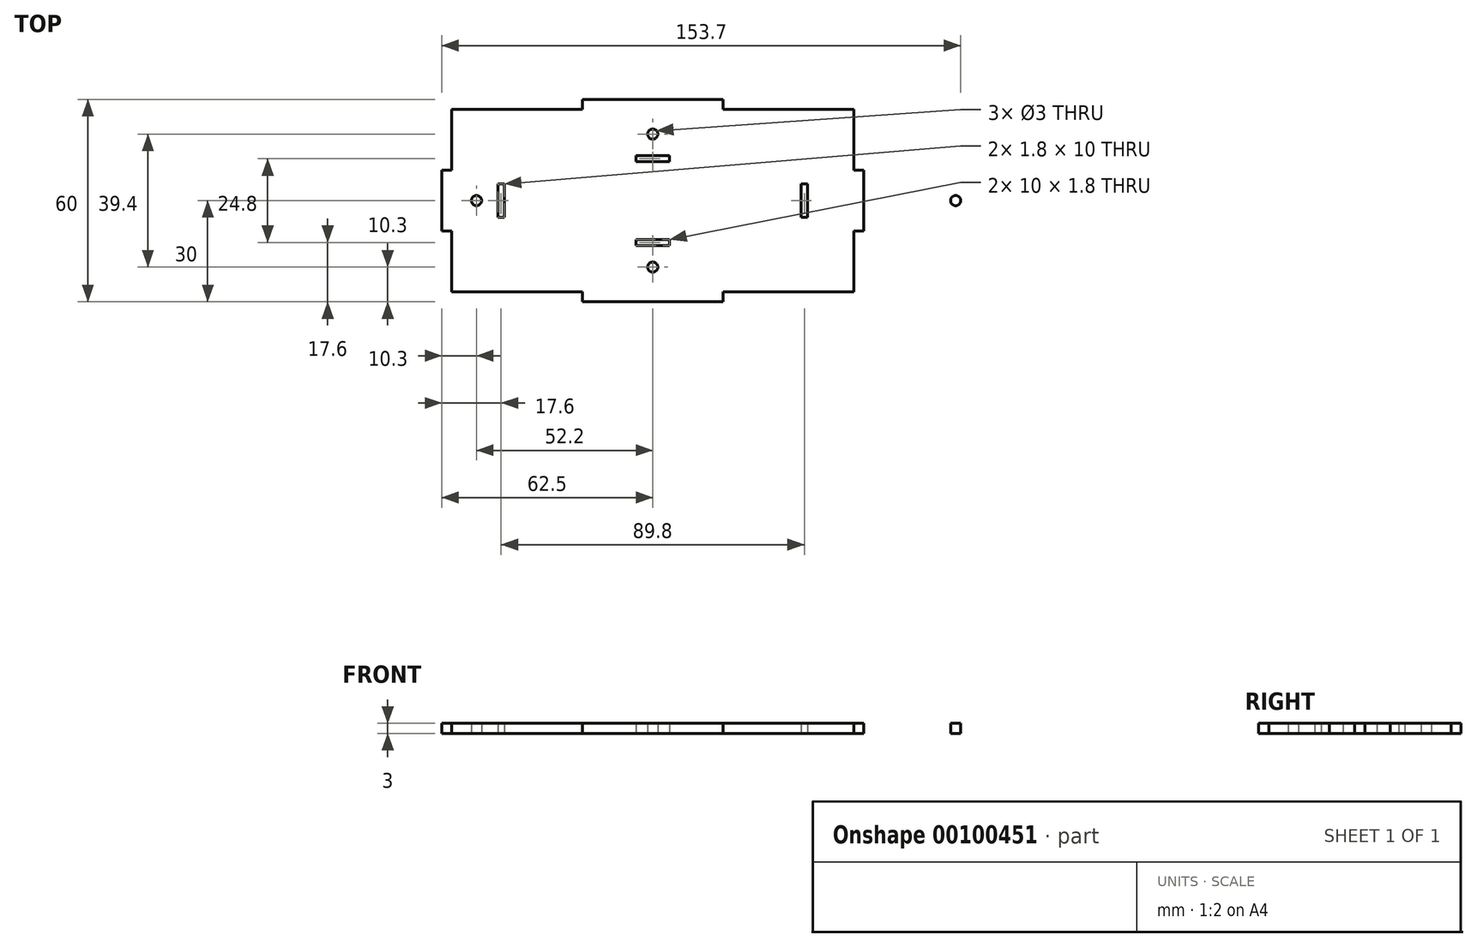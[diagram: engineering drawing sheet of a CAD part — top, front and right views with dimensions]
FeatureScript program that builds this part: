
annotation { "Feature Type Name" : "Feature", "Feature Type Description" : "" }
export const myFeature = defineFeature(function(context is Context, id is Id, definition is map)
    precondition{}
    {
        {
            var Q0;
            Q0=qCreatedBy(makeId("Top.planeOp"),FACE);
            var sketch = newSketch(context, id + "F0", { "sketchPlane" : qUnion([Q0])});
            skLineSegment(sketch, "E0.bottom", {"start": v(-59.5, 27) * mm, "end": v(-20.83, 27) * mm});
            skLineSegment(sketch, "E0.top", {"start": v(-59.5, -27) * mm, "end": v(-20.83, -27) * mm});
            skLineSegment(sketch, "E0.left", {"start": v(-59.5, 27) * mm, "end": v(-59.5, 9) * mm});
            skLineSegment(sketch, "E0.right", {"start": v(59.5, 27) * mm, "end": v(59.5, 9) * mm});
            skLineSegment(sketch, "E1.bottom", {"start": v(-59.5, 9) * mm, "end": v(-62.5, 9) * mm});
            skLineSegment(sketch, "E1.top", {"start": v(-59.5, -9) * mm, "end": v(-62.5, -9) * mm});
            skLineSegment(sketch, "E1.right", {"start": v(-62.5, 9) * mm, "end": v(-62.5, -9) * mm});
            skLineSegment(sketch, "E2.top", {"start": v(-20.83, 30) * mm, "end": v(20.83, 30) * mm});
            skLineSegment(sketch, "E2.left", {"start": v(-20.83, 27) * mm, "end": v(-20.83, 30) * mm});
            skLineSegment(sketch, "E2.right", {"start": v(20.83, 27) * mm, "end": v(20.83, 30) * mm});
            skLineSegment(sketch, "E3.bottom", {"start": v(59.5, 9) * mm, "end": v(62.5, 9) * mm});
            skLineSegment(sketch, "E3.top", {"start": v(59.5, -9) * mm, "end": v(62.5, -9) * mm});
            skLineSegment(sketch, "E3.right", {"start": v(62.5, 9) * mm, "end": v(62.5, -9) * mm});
            skLineSegment(sketch, "E4.top", {"start": v(20.83, -30) * mm, "end": v(-20.83, -30) * mm});
            skLineSegment(sketch, "E4.left", {"start": v(20.83, -27) * mm, "end": v(20.83, -30) * mm});
            skLineSegment(sketch, "E4.right", {"start": v(-20.83, -27) * mm, "end": v(-20.83, -30) * mm});
            skLineSegment(sketch, "E5.trimOffspring", {"start": v(20.83, 27) * mm, "end": v(59.5, 27) * mm});
            skLineSegment(sketch, "E6.trimOffspring", {"start": v(20.83, -27) * mm, "end": v(59.5, -27) * mm});
            skLineSegment(sketch, "E7.trimOffspring", {"start": v(-59.5, -9) * mm, "end": v(-59.5, -27) * mm});
            skLineSegment(sketch, "E8.trimOffspring", {"start": v(59.5, -9) * mm, "end": v(59.5, -27) * mm});
            skLineSegment(sketch, "E9", {"start": v(-62.5, 30) * mm, "end": v(-20.83, 30) * mm, "construction": true});
            skLineSegment(sketch, "E10", {"start": v(20.83, 30) * mm, "end": v(62.5, 30) * mm, "construction": true});
            skCircle(sketch, "E11", {"center": v(-52.2, 0) * mm, "radius": 1.5 * mm});
            skLineSegment(sketch, "E12.bottom", {"start": v(-45.8, 5) * mm, "end": v(-44, 5) * mm});
            skLineSegment(sketch, "E12.top", {"start": v(-45.8, -5) * mm, "end": v(-44, -5) * mm});
            skLineSegment(sketch, "E12.left", {"start": v(-45.8, 5) * mm, "end": v(-45.8, -5) * mm});
            skLineSegment(sketch, "E12.right", {"start": v(-44, 5) * mm, "end": v(-44, -5) * mm});
            skLineSegment(sketch, "E13.MirrorCS", {"start": v(45.8, 5) * mm, "end": v(44, 5) * mm});
            skLineSegment(sketch, "E14.MirrorCS", {"start": v(45.8, -5) * mm, "end": v(44, -5) * mm});
            skLineSegment(sketch, "E15.MirrorCS", {"start": v(44, 5) * mm, "end": v(44, -5) * mm});
            skLineSegment(sketch, "E16.MirrorCS", {"start": v(45.8, 5) * mm, "end": v(45.8, -5) * mm});
            skCircle(sketch, "E17.MirrorC", {"center": v(89.7, 0) * mm, "radius": 1.5 * mm});
            skCircle(sketch, "E18", {"center": v(0, 19.7) * mm, "radius": 1.5 * mm});
            skLineSegment(sketch, "E19.bottom", {"start": v(5, 13.3) * mm, "end": v(-5, 13.3) * mm});
            skLineSegment(sketch, "E19.top", {"start": v(5, 11.5) * mm, "end": v(-5, 11.5) * mm});
            skLineSegment(sketch, "E19.left", {"start": v(5, 13.3) * mm, "end": v(5, 11.5) * mm});
            skLineSegment(sketch, "E19.right", {"start": v(-5, 13.3) * mm, "end": v(-5, 11.5) * mm});
            skLineSegment(sketch, "E20.MirrorCS", {"start": v(-5, -13.3) * mm, "end": v(-5, -11.5) * mm});
            skLineSegment(sketch, "E21.MirrorCS", {"start": v(5, -13.3) * mm, "end": v(5, -11.5) * mm});
            skCircle(sketch, "E22.MirrorC", {"center": v(0, -19.7) * mm, "radius": 1.5 * mm});
            skLineSegment(sketch, "E23.MirrorCS", {"start": v(5, -11.5) * mm, "end": v(-5, -11.5) * mm});
            skLineSegment(sketch, "E24.MirrorCS", {"start": v(5, -13.3) * mm, "end": v(-5, -13.3) * mm});
            skSolve(sketch);
        }
        {
            var Q0;
            Q0=qSketchRegion(id+"F0",true);
            extrude(context, id + "F1", {"entities" : qUnion([Q0]), "depth" : 3 * mm});
        }
    });
